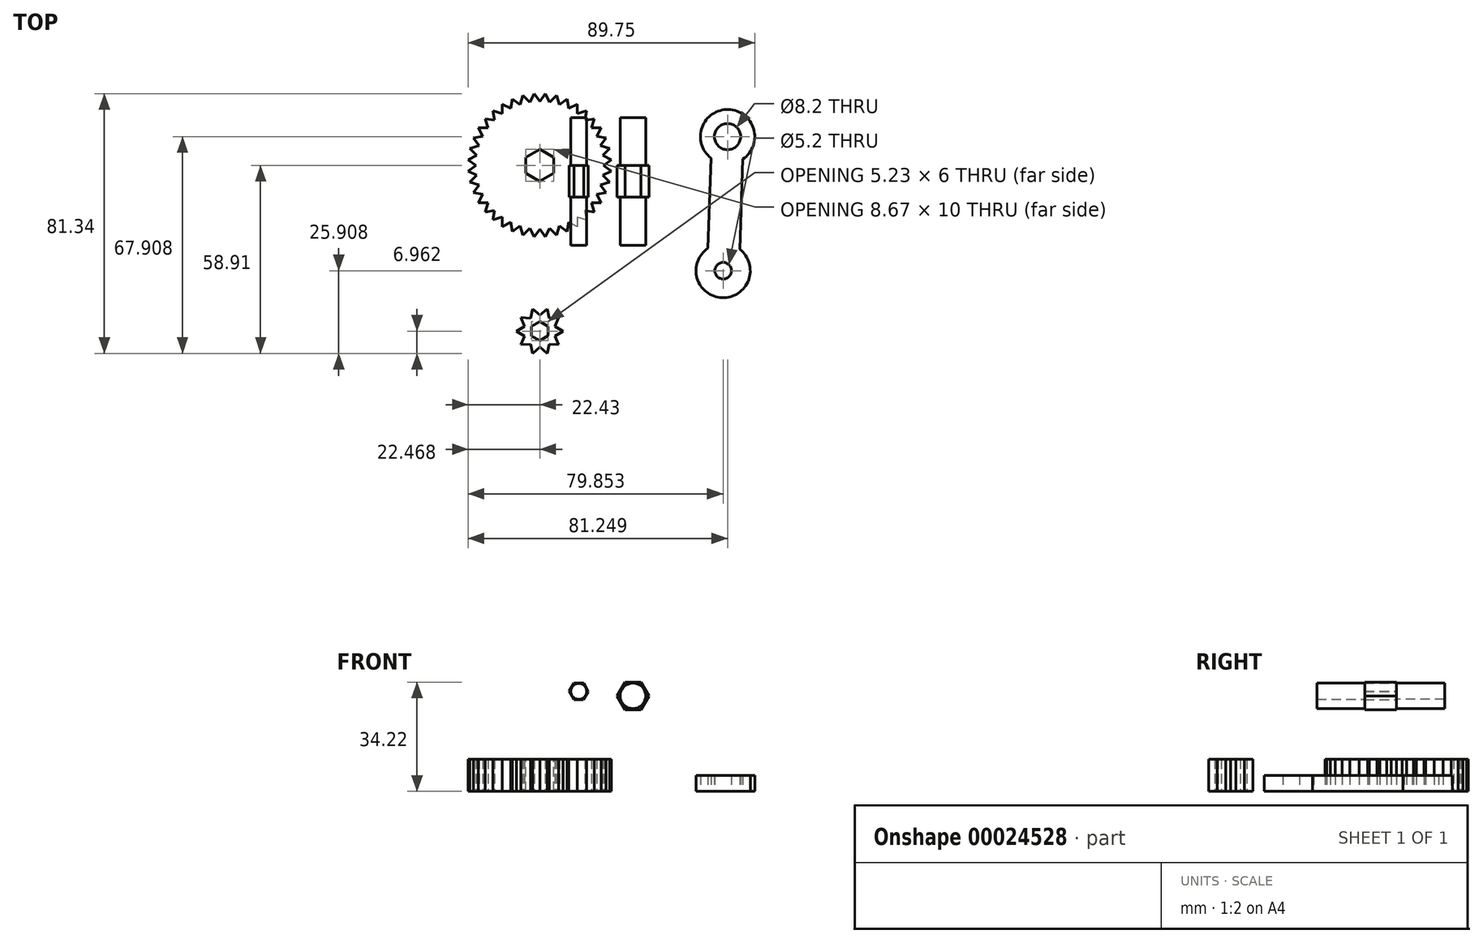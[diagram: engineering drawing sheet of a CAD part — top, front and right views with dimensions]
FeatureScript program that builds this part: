
annotation { "Feature Type Name" : "Feature", "Feature Type Description" : "" }
export const myFeature = defineFeature(function(context is Context, id is Id, definition is map)
    precondition{}
    {
        {
            var Q0;
            Q0=qCreatedBy(makeId("Top.planeOp"),FACE);
            var sketch = newSketch(context, id + "F0", { "sketchPlane" : qUnion([Q0])});
            skLineSegment(sketch, "E0", {"start": v(0, 20) * mm, "end": v(1.76, 22.43) * mm});
            skLineSegment(sketch, "E1", {"start": v(1.76, 22.43) * mm, "end": v(3.13, 19.75) * mm});
            skLineSegment(sketch, "E2.MirrorCS", {"start": v(6.18, 19.02) * mm, "end": v(5.25, 21.87) * mm});
            skLineSegment(sketch, "E3.MirrorCS", {"start": v(5.25, 21.87) * mm, "end": v(3.13, 19.75) * mm});
            skLineSegment(sketch, "E4.MirrorCS", {"start": v(6.18, 19.02) * mm, "end": v(8.6, 20.78) * mm});
            skLineSegment(sketch, "E5.MirrorCS", {"start": v(8.6, 20.78) * mm, "end": v(9.08, 17.82) * mm});
            skLineSegment(sketch, "E6.MirrorCS", {"start": v(11.75, 19.18) * mm, "end": v(9.08, 17.82) * mm});
            skLineSegment(sketch, "E7.MirrorCS", {"start": v(11.76, 16.18) * mm, "end": v(11.75, 19.18) * mm});
            skLineSegment(sketch, "E8.MirrorCS", {"start": v(14.6, 17.1) * mm, "end": v(14.14, 14.14) * mm});
            skLineSegment(sketch, "E9.MirrorCS", {"start": v(17.1, 14.6) * mm, "end": v(14.14, 14.14) * mm});
            skLineSegment(sketch, "E10.MirrorCS", {"start": v(11.76, 16.18) * mm, "end": v(14.6, 17.1) * mm});
            skLineSegment(sketch, "E11.MirrorCS", {"start": v(16.18, 11.76) * mm, "end": v(17.1, 14.6) * mm});
            skLineSegment(sketch, "E12.MirrorCS", {"start": v(16.18, 11.76) * mm, "end": v(19.18, 11.75) * mm});
            skLineSegment(sketch, "E13.MirrorCS", {"start": v(19.18, 11.75) * mm, "end": v(17.82, 9.08) * mm});
            skLineSegment(sketch, "E14.MirrorCS", {"start": v(19.02, 6.18) * mm, "end": v(20.78, 8.6) * mm});
            skLineSegment(sketch, "E15.MirrorCS", {"start": v(20.78, 8.6) * mm, "end": v(17.82, 9.08) * mm});
            skLineSegment(sketch, "E16.MirrorCS", {"start": v(19.02, 6.18) * mm, "end": v(21.87, 5.25) * mm});
            skLineSegment(sketch, "E17.MirrorCS", {"start": v(21.87, 5.25) * mm, "end": v(19.75, 3.13) * mm});
            skLineSegment(sketch, "E18.MirrorCS", {"start": v(11.76, -16.18) * mm, "end": v(14.6, -17.1) * mm});
            skLineSegment(sketch, "E19.MirrorCS", {"start": v(14.6, -17.1) * mm, "end": v(14.14, -14.14) * mm});
            skLineSegment(sketch, "E20.MirrorCS", {"start": v(17.1, -14.6) * mm, "end": v(14.14, -14.14) * mm});
            skLineSegment(sketch, "E21.MirrorCS", {"start": v(16.18, -11.76) * mm, "end": v(17.1, -14.6) * mm});
            skLineSegment(sketch, "E22.MirrorCS", {"start": v(16.18, -11.76) * mm, "end": v(19.18, -11.75) * mm});
            skLineSegment(sketch, "E23.MirrorCS", {"start": v(19.18, -11.75) * mm, "end": v(17.82, -9.08) * mm});
            skLineSegment(sketch, "E24.MirrorCS", {"start": v(20.78, -8.6) * mm, "end": v(17.82, -9.08) * mm});
            skLineSegment(sketch, "E25.MirrorCS", {"start": v(19.02, -6.18) * mm, "end": v(21.87, -5.25) * mm});
            skLineSegment(sketch, "E26.MirrorCS", {"start": v(21.87, -5.25) * mm, "end": v(19.75, -3.13) * mm});
            skLineSegment(sketch, "E27.MirrorCS", {"start": v(22.43, -1.76) * mm, "end": v(19.75, -3.13) * mm});
            skLineSegment(sketch, "E28.MirrorCS", {"start": v(20, 0) * mm, "end": v(22.43, -1.76) * mm});
            skLineSegment(sketch, "E29.MirrorCS", {"start": v(20, 0) * mm, "end": v(22.43, 1.76) * mm});
            skLineSegment(sketch, "E30.MirrorCS", {"start": v(22.43, 1.76) * mm, "end": v(19.75, 3.13) * mm});
            skLineSegment(sketch, "E31.MirrorCS", {"start": v(19.02, -6.18) * mm, "end": v(20.78, -8.6) * mm});
            skPoint(sketch, "E32.MirrorCS.end.orphan", {"position": v(6.18, 19.02) * mm});
            skPoint(sketch, "E32.MirrorCS.start.orphan", {"position": v(0, 0) * mm});
            skPoint(sketch, "E33.MirrorCS.end.orphan", {"position": v(16.18, 11.76) * mm});
            skLineSegment(sketch, "E34.MirrorCS", {"start": v(11.76, -16.18) * mm, "end": v(11.75, -19.18) * mm});
            skLineSegment(sketch, "E35.MirrorCS", {"start": v(11.75, -19.18) * mm, "end": v(9.08, -17.82) * mm});
            skLineSegment(sketch, "E36.MirrorCS", {"start": v(8.6, -20.78) * mm, "end": v(9.08, -17.82) * mm});
            skLineSegment(sketch, "E37.MirrorCS", {"start": v(6.18, -19.02) * mm, "end": v(8.6, -20.78) * mm});
            skLineSegment(sketch, "E38.MirrorCS", {"start": v(6.18, -19.02) * mm, "end": v(5.25, -21.87) * mm});
            skLineSegment(sketch, "E39.MirrorCS", {"start": v(5.25, -21.87) * mm, "end": v(3.13, -19.75) * mm});
            skLineSegment(sketch, "E40.MirrorCS", {"start": v(1.76, -22.43) * mm, "end": v(3.13, -19.75) * mm});
            skLineSegment(sketch, "E41.MirrorCS", {"start": v(0, -20) * mm, "end": v(1.76, -22.43) * mm});
            skLineSegment(sketch, "E42.MirrorCS", {"start": v(0, -20) * mm, "end": v(-1.76, -22.43) * mm});
            skLineSegment(sketch, "E43.MirrorCS", {"start": v(-1.76, -22.43) * mm, "end": v(-3.13, -19.75) * mm});
            skLineSegment(sketch, "E44.MirrorCS", {"start": v(-5.25, -21.87) * mm, "end": v(-3.13, -19.75) * mm});
            skLineSegment(sketch, "E45.MirrorCS", {"start": v(-6.18, -19.02) * mm, "end": v(-5.25, -21.87) * mm});
            skLineSegment(sketch, "E46.MirrorCS", {"start": v(-6.18, -19.02) * mm, "end": v(-8.6, -20.78) * mm});
            skLineSegment(sketch, "E47.MirrorCS", {"start": v(-8.6, -20.78) * mm, "end": v(-9.08, -17.82) * mm});
            skLineSegment(sketch, "E48.MirrorCS", {"start": v(-11.75, -19.18) * mm, "end": v(-9.08, -17.82) * mm});
            skLineSegment(sketch, "E49.MirrorCS", {"start": v(-11.76, -16.18) * mm, "end": v(-11.75, -19.18) * mm});
            skLineSegment(sketch, "E50.MirrorCS", {"start": v(-11.76, -16.18) * mm, "end": v(-14.6, -17.1) * mm});
            skLineSegment(sketch, "E51.MirrorCS", {"start": v(-14.6, -17.1) * mm, "end": v(-14.14, -14.14) * mm});
            skLineSegment(sketch, "E52.MirrorCS", {"start": v(-17.1, -14.6) * mm, "end": v(-14.14, -14.14) * mm});
            skLineSegment(sketch, "E53.MirrorCS", {"start": v(-16.18, -11.76) * mm, "end": v(-17.1, -14.6) * mm});
            skLineSegment(sketch, "E54.MirrorCS", {"start": v(-16.18, -11.76) * mm, "end": v(-19.18, -11.75) * mm});
            skLineSegment(sketch, "E55.MirrorCS", {"start": v(-20.78, -8.6) * mm, "end": v(-17.82, -9.08) * mm});
            skLineSegment(sketch, "E56.MirrorCS", {"start": v(-19.02, -6.18) * mm, "end": v(-20.78, -8.6) * mm});
            skLineSegment(sketch, "E57.MirrorCS", {"start": v(-19.02, -6.18) * mm, "end": v(-21.87, -5.25) * mm});
            skLineSegment(sketch, "E58.MirrorCS", {"start": v(-21.87, -5.25) * mm, "end": v(-19.75, -3.13) * mm});
            skLineSegment(sketch, "E59.MirrorCS", {"start": v(-22.43, -1.76) * mm, "end": v(-19.75, -3.13) * mm});
            skLineSegment(sketch, "E60.MirrorCS", {"start": v(-20, 0) * mm, "end": v(-22.43, -1.76) * mm});
            skLineSegment(sketch, "E61.MirrorCS", {"start": v(-20, 0) * mm, "end": v(-22.43, 1.76) * mm});
            skLineSegment(sketch, "E62.MirrorCS", {"start": v(-22.43, 1.76) * mm, "end": v(-19.75, 3.13) * mm});
            skLineSegment(sketch, "E63.MirrorCS", {"start": v(-19.02, 6.18) * mm, "end": v(-21.87, 5.25) * mm});
            skLineSegment(sketch, "E64.MirrorCS", {"start": v(-21.87, 5.25) * mm, "end": v(-19.75, 3.13) * mm});
            skLineSegment(sketch, "E65.MirrorCS", {"start": v(-19.02, 6.18) * mm, "end": v(-20.78, 8.6) * mm});
            skLineSegment(sketch, "E66.MirrorCS", {"start": v(-20.78, 8.6) * mm, "end": v(-17.82, 9.08) * mm});
            skLineSegment(sketch, "E67.MirrorCS", {"start": v(-19.18, 11.75) * mm, "end": v(-17.82, 9.08) * mm});
            skLineSegment(sketch, "E68.MirrorCS", {"start": v(-16.18, 11.76) * mm, "end": v(-19.18, 11.75) * mm});
            skLineSegment(sketch, "E69.MirrorCS", {"start": v(-16.18, 11.76) * mm, "end": v(-17.1, 14.6) * mm});
            skLineSegment(sketch, "E70.MirrorCS", {"start": v(-17.1, 14.6) * mm, "end": v(-14.14, 14.14) * mm});
            skLineSegment(sketch, "E71.MirrorCS", {"start": v(-14.6, 17.1) * mm, "end": v(-14.14, 14.14) * mm});
            skLineSegment(sketch, "E72.MirrorCS", {"start": v(-11.76, 16.18) * mm, "end": v(-14.6, 17.1) * mm});
            skLineSegment(sketch, "E73.MirrorCS", {"start": v(-11.76, 16.18) * mm, "end": v(-11.75, 19.18) * mm});
            skLineSegment(sketch, "E74.MirrorCS", {"start": v(-11.75, 19.18) * mm, "end": v(-9.08, 17.82) * mm});
            skLineSegment(sketch, "E75.MirrorCS", {"start": v(-6.18, 19.02) * mm, "end": v(-8.6, 20.78) * mm});
            skLineSegment(sketch, "E76.MirrorCS", {"start": v(-6.18, 19.02) * mm, "end": v(-5.25, 21.87) * mm});
            skLineSegment(sketch, "E77.MirrorCS", {"start": v(-5.25, 21.87) * mm, "end": v(-3.13, 19.75) * mm});
            skLineSegment(sketch, "E78.MirrorCS", {"start": v(-1.76, 22.43) * mm, "end": v(-3.13, 19.75) * mm});
            skLineSegment(sketch, "E79.MirrorCS", {"start": v(0, 20) * mm, "end": v(-1.76, 22.43) * mm});
            skLineSegment(sketch, "E80.MirrorCS", {"start": v(-8.6, 20.78) * mm, "end": v(-9.08, 17.82) * mm});
            skLineSegment(sketch, "E81.MirrorCS", {"start": v(-17.82, -9.08) * mm, "end": v(-19.18, -11.75) * mm});
            skSolve(sketch);
        }
        {
            var Q0;
            Q0=makeQuery(id+"F0.imprint","IMPRINT",FACE,{"disambiguationData":[TD([[makeQuery(id+"F0.imprint","IMPRINT",EDGE,{"derivedFrom":sQuery(id+"F0.wireOp",EDGE,"E0")}),-1.0]])]});
            extrude(context, id + "F1", {"entities" : qUnion([Q0]), "depth" : 10 * mm});
        }
        {
            var Q0;
            Q0=makeQuery(id+"F1.opExtrude","CAP_FACE",FACE,{"disambiguationData":[OSD([sQuery(id+"F0.wireOp",EDGE,"E0"),sQuery(id+"F0.wireOp",EDGE,"E1"),sQuery(id+"F0.wireOp",EDGE,"E2.MirrorCS"),sQuery(id+"F0.wireOp",EDGE,"E3.MirrorCS"),sQuery(id+"F0.wireOp",EDGE,"E4.MirrorCS"),sQuery(id+"F0.wireOp",EDGE,"E5.MirrorCS"),sQuery(id+"F0.wireOp",EDGE,"E6.MirrorCS"),sQuery(id+"F0.wireOp",EDGE,"E7.MirrorCS"),sQuery(id+"F0.wireOp",EDGE,"E8.MirrorCS"),sQuery(id+"F0.wireOp",EDGE,"E9.MirrorCS"),sQuery(id+"F0.wireOp",EDGE,"E10.MirrorCS"),sQuery(id+"F0.wireOp",EDGE,"E11.MirrorCS"),sQuery(id+"F0.wireOp",EDGE,"E12.MirrorCS"),sQuery(id+"F0.wireOp",EDGE,"E13.MirrorCS"),sQuery(id+"F0.wireOp",EDGE,"E14.MirrorCS"),sQuery(id+"F0.wireOp",EDGE,"E15.MirrorCS"),sQuery(id+"F0.wireOp",EDGE,"E16.MirrorCS"),sQuery(id+"F0.wireOp",EDGE,"E17.MirrorCS"),sQuery(id+"F0.wireOp",EDGE,"E18.MirrorCS"),sQuery(id+"F0.wireOp",EDGE,"E19.MirrorCS"),sQuery(id+"F0.wireOp",EDGE,"E20.MirrorCS"),sQuery(id+"F0.wireOp",EDGE,"E21.MirrorCS"),sQuery(id+"F0.wireOp",EDGE,"E22.MirrorCS"),sQuery(id+"F0.wireOp",EDGE,"E23.MirrorCS"),sQuery(id+"F0.wireOp",EDGE,"E24.MirrorCS"),sQuery(id+"F0.wireOp",EDGE,"E25.MirrorCS"),sQuery(id+"F0.wireOp",EDGE,"E26.MirrorCS"),sQuery(id+"F0.wireOp",EDGE,"E27.MirrorCS"),sQuery(id+"F0.wireOp",EDGE,"E29.MirrorCS"),sQuery(id+"F0.wireOp",EDGE,"E30.MirrorCS"),sQuery(id+"F0.wireOp",EDGE,"E28.MirrorCS"),sQuery(id+"F0.wireOp",EDGE,"E31.MirrorCS"),sQuery(id+"F0.wireOp",EDGE,"E34.MirrorCS"),sQuery(id+"F0.wireOp",EDGE,"E35.MirrorCS"),sQuery(id+"F0.wireOp",EDGE,"E36.MirrorCS"),sQuery(id+"F0.wireOp",EDGE,"E37.MirrorCS"),sQuery(id+"F0.wireOp",EDGE,"E38.MirrorCS"),sQuery(id+"F0.wireOp",EDGE,"E39.MirrorCS"),sQuery(id+"F0.wireOp",EDGE,"E40.MirrorCS"),sQuery(id+"F0.wireOp",EDGE,"E41.MirrorCS"),sQuery(id+"F0.wireOp",EDGE,"E42.MirrorCS"),sQuery(id+"F0.wireOp",EDGE,"E43.MirrorCS"),sQuery(id+"F0.wireOp",EDGE,"E44.MirrorCS"),sQuery(id+"F0.wireOp",EDGE,"E45.MirrorCS"),sQuery(id+"F0.wireOp",EDGE,"E46.MirrorCS"),sQuery(id+"F0.wireOp",EDGE,"E47.MirrorCS"),sQuery(id+"F0.wireOp",EDGE,"E48.MirrorCS"),sQuery(id+"F0.wireOp",EDGE,"E49.MirrorCS"),sQuery(id+"F0.wireOp",EDGE,"E50.MirrorCS"),sQuery(id+"F0.wireOp",EDGE,"E51.MirrorCS"),sQuery(id+"F0.wireOp",EDGE,"E52.MirrorCS"),sQuery(id+"F0.wireOp",EDGE,"E53.MirrorCS"),sQuery(id+"F0.wireOp",EDGE,"E54.MirrorCS"),sQuery(id+"F0.wireOp",EDGE,"E55.MirrorCS"),sQuery(id+"F0.wireOp",EDGE,"E56.MirrorCS"),sQuery(id+"F0.wireOp",EDGE,"E57.MirrorCS"),sQuery(id+"F0.wireOp",EDGE,"E58.MirrorCS"),sQuery(id+"F0.wireOp",EDGE,"E59.MirrorCS"),sQuery(id+"F0.wireOp",EDGE,"E60.MirrorCS"),sQuery(id+"F0.wireOp",EDGE,"E61.MirrorCS"),sQuery(id+"F0.wireOp",EDGE,"E62.MirrorCS"),sQuery(id+"F0.wireOp",EDGE,"E63.MirrorCS"),sQuery(id+"F0.wireOp",EDGE,"E64.MirrorCS"),sQuery(id+"F0.wireOp",EDGE,"E65.MirrorCS"),sQuery(id+"F0.wireOp",EDGE,"E66.MirrorCS"),sQuery(id+"F0.wireOp",EDGE,"E67.MirrorCS"),sQuery(id+"F0.wireOp",EDGE,"E68.MirrorCS"),sQuery(id+"F0.wireOp",EDGE,"E70.MirrorCS"),sQuery(id+"F0.wireOp",EDGE,"E69.MirrorCS"),sQuery(id+"F0.wireOp",EDGE,"E71.MirrorCS"),sQuery(id+"F0.wireOp",EDGE,"E72.MirrorCS"),sQuery(id+"F0.wireOp",EDGE,"E73.MirrorCS"),sQuery(id+"F0.wireOp",EDGE,"E74.MirrorCS"),sQuery(id+"F0.wireOp",EDGE,"E75.MirrorCS"),sQuery(id+"F0.wireOp",EDGE,"E76.MirrorCS"),sQuery(id+"F0.wireOp",EDGE,"E77.MirrorCS"),sQuery(id+"F0.wireOp",EDGE,"E78.MirrorCS"),sQuery(id+"F0.wireOp",EDGE,"E79.MirrorCS"),sQuery(id+"F0.wireOp",EDGE,"E80.MirrorCS"),sQuery(id+"F0.wireOp",EDGE,"E81.MirrorCS")])],"isStart":false});
            var sketch = newSketch(context, id + "F2", { "sketchPlane" : qUnion([Q0])});
            skCircle(sketch, "E82.cCircle", {"center": v(0, 0) * mm, "radius": 4.33 * mm, "construction": true});
            skLineSegment(sketch, "E82.0", {"start": v(4.32, -2.51) * mm, "end": v(-0.01, -5) * mm});
            skLineSegment(sketch, "E82.1", {"start": v(-0.01, -5) * mm, "end": v(-4.34, -2.49) * mm});
            skLineSegment(sketch, "E82.2", {"start": v(-4.34, -2.49) * mm, "end": v(-4.32, 2.51) * mm});
            skLineSegment(sketch, "E82.3", {"start": v(-4.32, 2.51) * mm, "end": v(0.01, 5) * mm});
            skLineSegment(sketch, "E82.4", {"start": v(0.01, 5) * mm, "end": v(4.34, 2.49) * mm});
            skLineSegment(sketch, "E82.5", {"start": v(4.34, 2.49) * mm, "end": v(4.32, -2.51) * mm});
            skPoint(sketch, "E82.0.midPoint", {"position": v(2.16, -3.76) * mm});
            skSolve(sketch);
        }
        {
            var Q0;
            Q0=makeQuery(id+"F2.imprint","IMPRINT",FACE,{"disambiguationData":[TD([[makeQuery(id+"F2.imprint","IMPRINT",EDGE,{"derivedFrom":sQuery(id+"F2.wireOp",EDGE,"E82.0")}),-1.0]])]});
            extrude(context, id + "F3", {"entities" : qUnion([Q0]), "operationType" : NewBodyOperationType.REMOVE, "oppositeDirection" : true, "depth" : 10 * mm});
        }
        {
            var Q0;
            Q0=qCreatedBy(makeId("Top.planeOp"),FACE);
            var sketch = newSketch(context, id + "F4", { "sketchPlane" : qUnion([Q0])});
            skLineSegment(sketch, "E83", {"start": v(0.04, -46.95) * mm, "end": v(2.31, -45) * mm});
            skLineSegment(sketch, "E84", {"start": v(2.31, -45) * mm, "end": v(2.96, -47.92) * mm});
            skLineSegment(sketch, "E85.MirrorCS", {"start": v(5.95, -47.64) * mm, "end": v(2.96, -47.92) * mm});
            skLineSegment(sketch, "E86.MirrorCS", {"start": v(4.8, -50.4) * mm, "end": v(5.95, -47.64) * mm});
            skLineSegment(sketch, "E87.MirrorCS", {"start": v(2.98, -56) * mm, "end": v(5.97, -56.24) * mm});
            skLineSegment(sketch, "E88.MirrorCS", {"start": v(5.97, -56.24) * mm, "end": v(4.77, -53.49) * mm});
            skLineSegment(sketch, "E89.MirrorCS", {"start": v(7.36, -51.96) * mm, "end": v(4.77, -53.49) * mm});
            skLineSegment(sketch, "E90.MirrorCS", {"start": v(4.8, -50.4) * mm, "end": v(7.36, -51.96) * mm});
            skLineSegment(sketch, "E91.MirrorCS", {"start": v(-4.72, -50.4) * mm, "end": v(-7.28, -51.96) * mm});
            skLineSegment(sketch, "E92.MirrorCS", {"start": v(-7.28, -51.96) * mm, "end": v(-4.7, -53.49) * mm});
            skLineSegment(sketch, "E93.MirrorCS", {"start": v(-5.9, -56.24) * mm, "end": v(-4.7, -53.49) * mm});
            skLineSegment(sketch, "E94.MirrorCS", {"start": v(-2.9, -56) * mm, "end": v(-5.9, -56.24) * mm});
            skLineSegment(sketch, "E95.MirrorCS", {"start": v(-2.9, -56) * mm, "end": v(-2.21, -58.91) * mm});
            skLineSegment(sketch, "E96.MirrorCS", {"start": v(-2.21, -58.91) * mm, "end": v(0.04, -56.93) * mm});
            skLineSegment(sketch, "E97.MirrorCS", {"start": v(2.29, -58.91) * mm, "end": v(0.04, -56.93) * mm});
            skLineSegment(sketch, "E98.MirrorCS", {"start": v(2.98, -56) * mm, "end": v(2.29, -58.91) * mm});
            skLineSegment(sketch, "E99.MirrorCS", {"start": v(-4.72, -50.4) * mm, "end": v(-5.87, -47.64) * mm});
            skLineSegment(sketch, "E100.MirrorCS", {"start": v(-5.87, -47.64) * mm, "end": v(-2.89, -47.92) * mm});
            skLineSegment(sketch, "E101.MirrorCS", {"start": v(-2.24, -45) * mm, "end": v(-2.89, -47.92) * mm});
            skLineSegment(sketch, "E102.MirrorCS", {"start": v(0.04, -46.95) * mm, "end": v(-2.24, -45) * mm});
            skPoint(sketch, "E103.MirrorCS.end.orphan", {"position": v(0.04, -51.95) * mm});
            skPoint(sketch, "E103.MirrorCS.start.orphan", {"position": v(-4.72, -50.4) * mm});
            skPoint(sketch, "E104.center.orphan", {"position": v(0, -51.95) * mm});
            skCircle(sketch, "E105.cCircle", {"center": v(0.04, -51.95) * mm, "radius": 2.6 * mm, "construction": true});
            skLineSegment(sketch, "E105.0", {"start": v(0, -48.95) * mm, "end": v(2.62, -50.42) * mm});
            skLineSegment(sketch, "E105.1", {"start": v(2.62, -50.42) * mm, "end": v(2.65, -53.42) * mm});
            skLineSegment(sketch, "E105.2", {"start": v(2.65, -53.42) * mm, "end": v(0.07, -54.95) * mm});
            skLineSegment(sketch, "E105.3", {"start": v(0.07, -54.95) * mm, "end": v(-2.54, -53.48) * mm});
            skLineSegment(sketch, "E105.4", {"start": v(-2.54, -53.48) * mm, "end": v(-2.58, -50.48) * mm});
            skLineSegment(sketch, "E105.5", {"start": v(-2.58, -50.48) * mm, "end": v(0, -48.95) * mm});
            skPoint(sketch, "E105.0.midPoint", {"position": v(1.31, -49.68) * mm});
            skSolve(sketch);
        }
        {
            var Q0;
            Q0=makeQuery(id+"F4.imprint","IMPRINT",FACE,{"disambiguationData":[TD([[makeQuery(id+"F4.imprint","IMPRINT",EDGE,{"derivedFrom":sQuery(id+"F4.wireOp",EDGE,"E83")}),-1.0]])]});
            extrude(context, id + "F5", {"entities" : qUnion([Q0]), "depth" : 10 * mm});
        }
        {
            var Q0;
            Q0=qCreatedBy(makeId("Top.planeOp"),FACE);
            var sketch = newSketch(context, id + "F6", { "sketchPlane" : qUnion([Q0])});
            skCircle(sketch, "E106", {"center": v(58.82, 9) * mm, "radius": 4.1 * mm});
            skCircle(sketch, "E107", {"center": v(58.82, 9) * mm, "radius": 8.5 * mm});
            skCircle(sketch, "E108", {"center": v(57.42, -33) * mm, "radius": 2.6 * mm});
            skCircle(sketch, "E109", {"center": v(57.42, -33) * mm, "radius": 8.5 * mm});
            skLineSegment(sketch, "E110", {"start": v(58.82, 9) * mm, "end": v(58.54, 0.5) * mm});
            skLineSegment(sketch, "E111", {"start": v(63.59, 1.96) * mm, "end": v(62.65, -26.3) * mm});
            skLineSegment(sketch, "E112.MirrorCS", {"start": v(53.6, 2.3) * mm, "end": v(52.65, -25.97) * mm});
            skLineSegment(sketch, "E113.trimOffspring", {"start": v(57.7, -24.5) * mm, "end": v(57.42, -33) * mm});
            skSolve(sketch);
        }
        {
            var Q0;
            Q0=makeQuery(id+"F6.imprint","IMPRINT",FACE,{"disambiguationData":[TD([[makeQuery(id+"F6.imprint","IMPRINT",EDGE,{"derivedFrom":sQuery(id+"F6.wireOp",EDGE,"E106")}),-1.0]])]});
            var Q1;
            {var subQ1=sQuery(id+"F6.wireOp",EDGE,"E111");Q1=makeQuery(id+"F6.imprint","IMPRINT",FACE,{"disambiguationData":[TD([[makeQuery(id+"F6.imprint","IMPRINT",EDGE,{"derivedFrom":subQ1}),-1.0]])]});}
            var Q2;
            Q2=makeQuery(id+"F6.imprint","IMPRINT",FACE,{"disambiguationData":[TD([[makeQuery(id+"F6.imprint","IMPRINT",EDGE,{"derivedFrom":sQuery(id+"F6.wireOp",EDGE,"E108")}),-1.0]])]});
            extrude(context, id + "F7", {"entities" : qUnion([Q0, Q1, Q2]), "depth" : 5 * mm});
        }
        {
            var Q0;
            Q0=qCreatedBy(makeId("Front.planeOp"),FACE);
            var sketch = newSketch(context, id + "F8", { "sketchPlane" : qUnion([Q0])});
            skCircle(sketch, "E114.cCircle", {"center": v(29.18, 29.9) * mm, "radius": 4.33 * mm, "construction": true});
            skLineSegment(sketch, "E114.0", {"start": v(31.68, 34.22) * mm, "end": v(34.18, 29.9) * mm});
            skLineSegment(sketch, "E114.1", {"start": v(34.18, 29.9) * mm, "end": v(31.68, 25.56) * mm});
            skLineSegment(sketch, "E114.2", {"start": v(31.68, 25.56) * mm, "end": v(26.68, 25.56) * mm});
            skLineSegment(sketch, "E114.3", {"start": v(26.68, 25.56) * mm, "end": v(24.18, 29.9) * mm});
            skLineSegment(sketch, "E114.4", {"start": v(24.18, 29.9) * mm, "end": v(26.68, 34.22) * mm});
            skLineSegment(sketch, "E114.5", {"start": v(26.68, 34.22) * mm, "end": v(31.68, 34.22) * mm});
            skPoint(sketch, "E114.0.midPoint", {"position": v(32.93, 32.06) * mm});
            skSolve(sketch);
        }
        {
            var Q0;
            Q0=makeQuery(id+"F8.imprint","IMPRINT",FACE,{"disambiguationData":[TD([[makeQuery(id+"F8.imprint","IMPRINT",EDGE,{"derivedFrom":sQuery(id+"F8.wireOp",EDGE,"E114.0")}),-1.0]])]});
            extrude(context, id + "F9", {"entities" : qUnion([Q0]), "depth" : 10 * mm});
        }
        {
            var Q0;
            Q0=makeQuery(id+"F9.opExtrude","CAP_FACE",FACE,{"disambiguationData":[OSD([sQuery(id+"F8.wireOp",EDGE,"E114.0"),sQuery(id+"F8.wireOp",EDGE,"E114.1"),sQuery(id+"F8.wireOp",EDGE,"E114.2"),sQuery(id+"F8.wireOp",EDGE,"E114.3"),sQuery(id+"F8.wireOp",EDGE,"E114.4"),sQuery(id+"F8.wireOp",EDGE,"E114.5")])],"isStart":false});
            var sketch = newSketch(context, id + "F10", { "sketchPlane" : qUnion([Q0])});
            skCircle(sketch, "E115", {"center": v(29.19, 29.9) * mm, "radius": 4 * mm});
            skSolve(sketch);
        }
        {
            var Q0;
            Q0=makeQuery(id+"F10.imprint","IMPRINT",FACE,{"disambiguationData":[TD([[makeQuery(id+"F10.imprint","IMPRINT",EDGE,{"derivedFrom":sQuery(id+"F10.wireOp",EDGE,"E115")}),1.0]])]});
            extrude(context, id + "F11", {"entities" : qUnion([Q0]), "operationType" : NewBodyOperationType.ADD, "depth" : 15 * mm});
        }
        {
            var Q0;
            Q0=makeQuery(id+"F8.imprint","IMPRINT",FACE,{"disambiguationData":[TD([[makeQuery(id+"F8.imprint","IMPRINT",EDGE,{"derivedFrom":sQuery(id+"F8.wireOp",EDGE,"E114.0")}),-1.0]])]});
            var sketch = newSketch(context, id + "F12", { "sketchPlane" : qUnion([Q0])});
            skCircle(sketch, "E116", {"center": v(29.19, 29.9) * mm, "radius": 4 * mm});
            skSolve(sketch);
        }
        {
            var Q0;
            Q0=makeQuery(id+"F12.imprint","IMPRINT",FACE,{"disambiguationData":[TD([[makeQuery(id+"F12.imprint","IMPRINT",EDGE,{"derivedFrom":sQuery(id+"F12.wireOp",EDGE,"E116")}),1.0]])]});
            extrude(context, id + "F13", {"entities" : qUnion([Q0]), "operationType" : NewBodyOperationType.ADD, "oppositeDirection" : true, "depth" : 15 * mm});
        }
        {
            var Q0;
            Q0=qCreatedBy(makeId("Front.planeOp"),FACE);
            var sketch = newSketch(context, id + "F14", { "sketchPlane" : qUnion([Q0])});
            skCircle(sketch, "E117.cCircle", {"center": v(12.21, 31.3) * mm, "radius": 2.6 * mm, "construction": true});
            skLineSegment(sketch, "E117.0", {"start": v(13.75, 33.88) * mm, "end": v(15.21, 31.26) * mm});
            skLineSegment(sketch, "E117.1", {"start": v(15.21, 31.26) * mm, "end": v(13.68, 28.68) * mm});
            skLineSegment(sketch, "E117.2", {"start": v(13.68, 28.68) * mm, "end": v(10.68, 28.72) * mm});
            skLineSegment(sketch, "E117.3", {"start": v(10.68, 28.72) * mm, "end": v(9.21, 31.34) * mm});
            skLineSegment(sketch, "E117.4", {"start": v(9.21, 31.34) * mm, "end": v(10.75, 33.92) * mm});
            skLineSegment(sketch, "E117.5", {"start": v(10.75, 33.92) * mm, "end": v(13.75, 33.88) * mm});
            skPoint(sketch, "E117.0.midPoint", {"position": v(14.48, 32.57) * mm});
            skSolve(sketch);
        }
        {
            var Q0;
            Q0=makeQuery(id+"F14.imprint","IMPRINT",FACE,{"disambiguationData":[TD([[makeQuery(id+"F14.imprint","IMPRINT",EDGE,{"derivedFrom":sQuery(id+"F14.wireOp",EDGE,"E117.0")}),-1.0]])]});
            extrude(context, id + "F15", {"entities" : qUnion([Q0]), "depth" : 10 * mm});
        }
        {
            var Q0;
            Q0=makeQuery(id+"F15.opExtrude","CAP_FACE",FACE,{"disambiguationData":[OSD([sQuery(id+"F14.wireOp",EDGE,"E117.0"),sQuery(id+"F14.wireOp",EDGE,"E117.1"),sQuery(id+"F14.wireOp",EDGE,"E117.2"),sQuery(id+"F14.wireOp",EDGE,"E117.3"),sQuery(id+"F14.wireOp",EDGE,"E117.4"),sQuery(id+"F14.wireOp",EDGE,"E117.5")])],"isStart":false});
            var sketch = newSketch(context, id + "F16", { "sketchPlane" : qUnion([Q0])});
            skCircle(sketch, "E118", {"center": v(12.22, 31.3) * mm, "radius": 2.5 * mm});
            skSolve(sketch);
        }
        {
            var Q0;
            Q0=makeQuery(id+"F16.imprint","IMPRINT",FACE,{"disambiguationData":[TD([[makeQuery(id+"F16.imprint","IMPRINT",EDGE,{"derivedFrom":sQuery(id+"F16.wireOp",EDGE,"E118")}),1.0]])]});
            extrude(context, id + "F17", {"entities" : qUnion([Q0]), "operationType" : NewBodyOperationType.ADD, "depth" : 15 * mm});
        }
        {
            var Q0;
            Q0=makeQuery(id+"F14.imprint","IMPRINT",FACE,{"disambiguationData":[TD([[makeQuery(id+"F14.imprint","IMPRINT",EDGE,{"derivedFrom":sQuery(id+"F14.wireOp",EDGE,"E117.0")}),-1.0]])]});
            var sketch = newSketch(context, id + "F18", { "sketchPlane" : qUnion([Q0])});
            skCircle(sketch, "E119", {"center": v(12.22, 31.3) * mm, "radius": 2.5 * mm});
            skSolve(sketch);
        }
        {
            var Q0;
            Q0=makeQuery(id+"F18.imprint","IMPRINT",FACE,{"disambiguationData":[TD([[makeQuery(id+"F18.imprint","IMPRINT",EDGE,{"derivedFrom":sQuery(id+"F18.wireOp",EDGE,"E119")}),1.0]])]});
            extrude(context, id + "F19", {"entities" : qUnion([Q0]), "operationType" : NewBodyOperationType.ADD, "oppositeDirection" : true, "depth" : 15 * mm});
        }
    });
